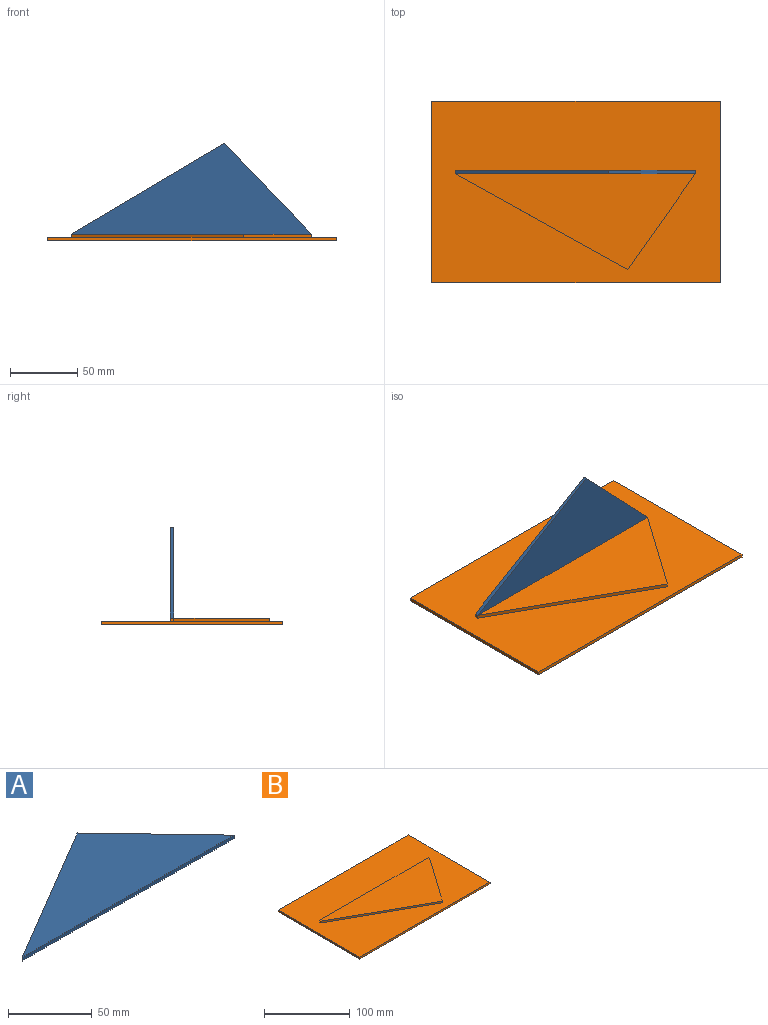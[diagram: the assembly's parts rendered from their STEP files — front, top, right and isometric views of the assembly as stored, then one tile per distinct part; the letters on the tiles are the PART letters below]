
ASSEMBLY  parts=2 mates=1
PART A: 5 faces, bbox 178.7x67.6x2.5 mm
  f0: plane 67.64x64.51mm, normal (0.72,0.69,0), area 237.4mm2, adj f1,f2,f3,f4
  f1: plane 114.21x67.64mm, normal (-0.51,0.86,0), area 337.1mm2, adj f0,f2,f3,f4
  f2: plane 178.72x2.54mm, normal (0,-1,0), area 453.9mm2, adj f0,f1,f3,f4
  f3: plane 178.72x67.64mm, normal (0,0,1), area 6044mm2, adj f0,f1,f2
  f4: plane 178.72x67.64mm, normal (0,0,-1), area 6044mm2, adj f0,f1,f2
PART B: 12 faces, bbox 214.3x134.9x5.1 mm
  f0: plane 134.88x2.54mm, normal (-1,0,0), area 342.6mm2, adj f1,f3,f4,f5
  f1: plane 214.28x2.54mm, normal (0,-1,0), area 544.3mm2, adj f0,f2,f4,f5
  f2: plane 134.88x2.54mm, normal (1,0,0), area 342.6mm2, adj f1,f3,f4,f5
  f3: plane 214.28x2.54mm, normal (0,1,0), area 544.3mm2, adj f0,f2,f4,f5
  f4: plane 214.28x134.88mm, normal (0,0,1), area 22093.4mm2, adj f0,f1,f2,f3,f7,f8,f9,f10
  f5: plane 214.28x134.88mm, normal (0,0,-1), area 28902.6mm2, adj f0,f1,f2,f3
  f6: plane 178.72x73.66mm, normal (0,0,1), area 6809.2mm2, adj f7,f8,f9,f10,f11
  f7: plane 2.54x2.54mm, normal (-1,0,0), area 6.5mm2, adj f4,f6,f8,f11
  f8: plane 128.45x71.12mm, normal (-0.48,-0.87,0), area 372.9mm2, adj f4,f6,f7,f9
  f9: plane 71.12x50.27mm, normal (0.82,-0.58,0), area 221.2mm2, adj f4,f6,f8,f10
  f10: plane 2.54x2.54mm, normal (1,0,0), area 6.5mm2, adj f4,f6,f9,f11
  f11: plane 178.72x2.54mm, normal (0,1,0), area 453.9mm2, adj f4,f6,f7,f10
PLACE A rot(axis=(1,0,0),90deg) t=(4.36,13.73,-12.13)mm
PLACE B at identity
MATE fastened A.f2 <-> B.f6  axis (0,0,-1) through (-0.61,12.46,5.08)mm
